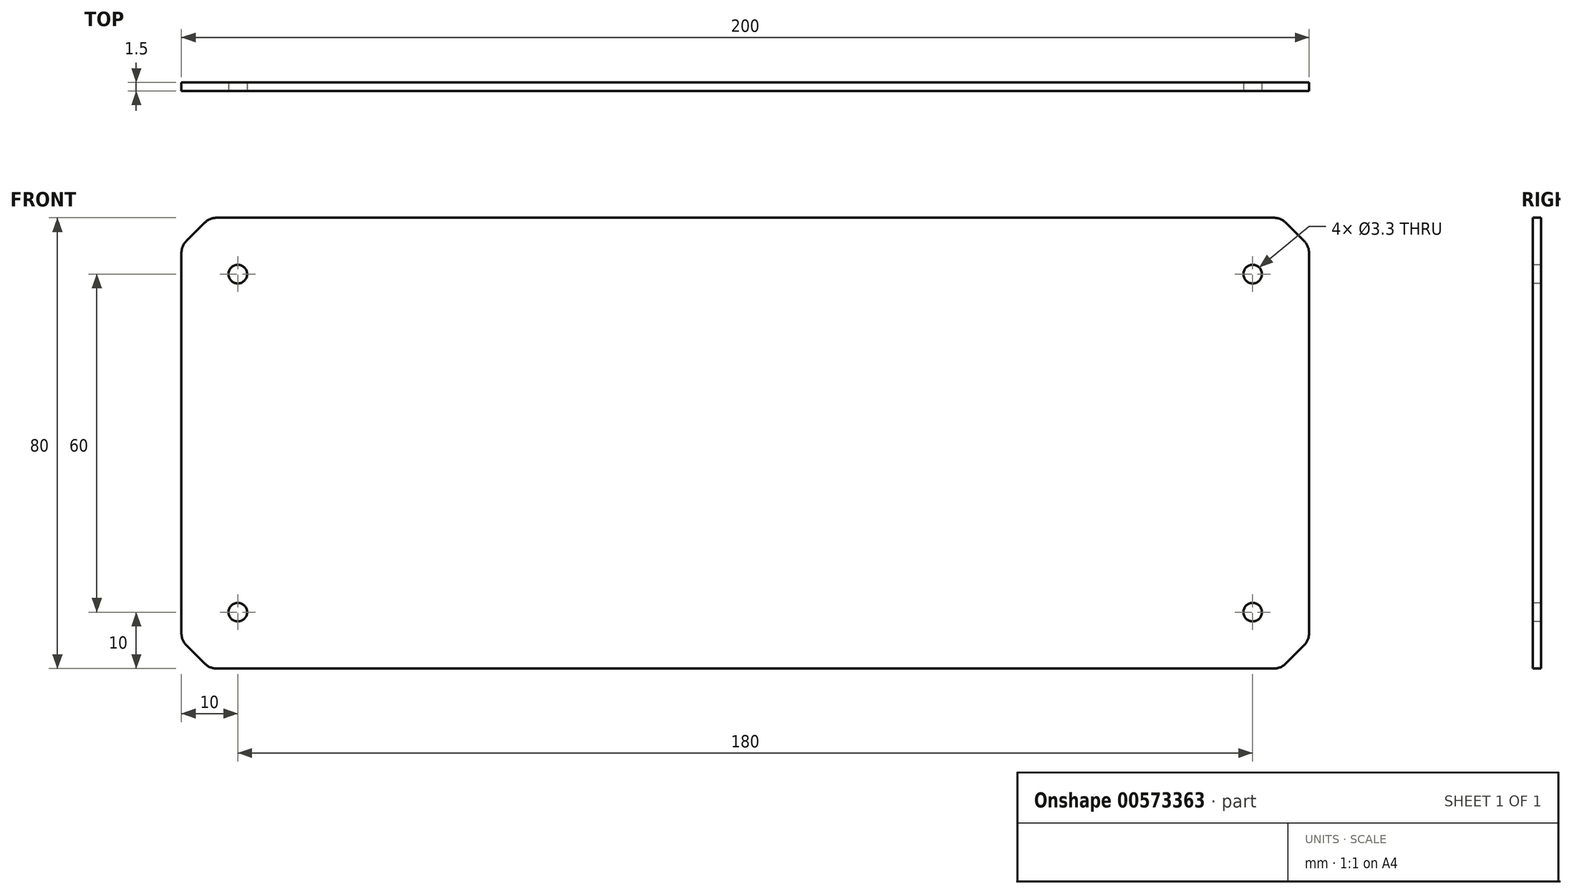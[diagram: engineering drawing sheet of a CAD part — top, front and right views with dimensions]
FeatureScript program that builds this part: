
annotation { "Feature Type Name" : "Feature", "Feature Type Description" : "" }
export const myFeature = defineFeature(function(context is Context, id is Id, definition is map)
    precondition{}
    {
        {
            var Q0;
            Q0=qCreatedBy(makeId("Front.planeOp"),FACE);
            var sketch = newSketch(context, id + "F0", { "sketchPlane" : qUnion([Q0])});
            skLineSegment(sketch, "E0.bottom", {"start": v(100, 40) * mm, "end": v(-100, 40) * mm});
            skLineSegment(sketch, "E0.top", {"start": v(100, -40) * mm, "end": v(-100, -40) * mm});
            skLineSegment(sketch, "E0.left", {"start": v(100, 40) * mm, "end": v(100, -40) * mm});
            skLineSegment(sketch, "E0.right", {"start": v(-100, 40) * mm, "end": v(-100, -40) * mm});
            skPoint(sketch, "E0.middle", {"position": v(0, 0) * mm});
            skSolve(sketch);
        }
        {
            var Q0;
            Q0 = qSketchRegion(id + "F0", true);
            extrude(context, id + "F1", {"entities" : qUnion([Q0]), "depth" : 1.5 * mm, "offsetDistance" : 25.4 * mm});
        }
        {
            var Q0;
            Q0=makeQuery(id+"F1.opExtrude","SWEPT_EDGE",EDGE,{"disambiguationData":[OSD([sQuery(id+"F0.wireOp",EDGE,"E0.bottom"),sQuery(id+"F0.wireOp",EDGE,"E0.left")])]});
            var Q1;
            Q1=makeQuery(id+"F1.opExtrude","SWEPT_EDGE",EDGE,{"disambiguationData":[OSD([sQuery(id+"F0.wireOp",EDGE,"E0.bottom"),sQuery(id+"F0.wireOp",EDGE,"E0.right")])]});
            var Q2;
            Q2=makeQuery(id+"F1.opExtrude","SWEPT_EDGE",EDGE,{"disambiguationData":[OSD([sQuery(id+"F0.wireOp",EDGE,"E0.top"),sQuery(id+"F0.wireOp",EDGE,"E0.right")])]});
            var Q3;
            Q3=makeQuery(id+"F1.opExtrude","SWEPT_EDGE",EDGE,{"disambiguationData":[OSD([sQuery(id+"F0.wireOp",EDGE,"E0.top"),sQuery(id+"F0.wireOp",EDGE,"E0.left")])]});
            chamfer(context, id + "F2", {"entities" : qUnion([Q0, Q1, Q2, Q3]), "width" : 5 * mm, "tangentPropagation" : true});
        }
        {
            var Q0;
            Q0=makeQuery(id+"F1.opExtrude","CAP_FACE",FACE,{"disambiguationData":[OSD([sQuery(id+"F0.wireOp",EDGE,"E0.bottom"),sQuery(id+"F0.wireOp",EDGE,"E0.top"),sQuery(id+"F0.wireOp",EDGE,"E0.left"),sQuery(id+"F0.wireOp",EDGE,"E0.right")])],"isStart":false});
            var sketch = newSketch(context, id + "F3", { "sketchPlane" : qUnion([Q0])});
            skPoint(sketch, "E1", {"position": v(-90, 30) * mm});
            skPoint(sketch, "E2", {"position": v(90, 30) * mm});
            skPoint(sketch, "E3", {"position": v(90, -30) * mm});
            skPoint(sketch, "E4", {"position": v(-90, -30) * mm});
            skSolve(sketch);
        }
        {
            var Q0;
            Q0=sQuery(id+"F3.wireOp",VERTEX,"E1");
            var Q1;
            Q1=sQuery(id+"F3.wireOp",VERTEX,"E4");
            var Q2;
            Q2=sQuery(id+"F3.wireOp",VERTEX,"E3");
            var Q3;
            Q3=sQuery(id+"F3.wireOp",VERTEX,"E2");
            var Q4;
            Q4=makeQuery(id+"F1.opExtrude","SWEPT_BODY",BODY,{"disambiguationData":[OSD([sQuery(id+"F0.wireOp",EDGE,"E0.bottom"),sQuery(id+"F0.wireOp",EDGE,"E0.top"),sQuery(id+"F0.wireOp",EDGE,"E0.left"),sQuery(id+"F0.wireOp",EDGE,"E0.right")])]});
            hole(context, id + "F4", {"style" : HoleStyle.SIMPLE, "endStyle" : HoleEndStyle.THROUGH, "standardTappedOrClearance" : lookupTablePath({ "standard" : "ISO", "fit" : "Normal", "size" : "M3", "type" : "Clearance" }), "standardBlindInLast" : lookupTablePath({ "fit" : "Standard", "standard" : "ISO", "size" : "M3", "type" : "Clearance" }), "holeDiameter" : 3.3 * mm, "isTappedThrough" : true, "tappedDepth" : 12 * mm, "tapClearance" : 3, "locations" : qUnion([Q0, Q1, Q2, Q3]), "scope" : qUnion([Q4])});
        }
        {
            var Q0;
            {var subQ0=sQuery(id+"F0.wireOp",EDGE,"E0.bottom");Q0=makeQuery(id+"F2.opChamfer","BLEND_EDGE",EDGE,{"blendedFrom":[makeQuery(id+"F1.opExtrude","SWEPT_EDGE",EDGE,{"disambiguationData":[OSD([subQ0,sQuery(id+"F0.wireOp",EDGE,"E0.left")])]}),makeQuery(id+"F1.opExtrude","SWEPT_FACE",FACE,{"disambiguationData":[OSD([subQ0])]})],"blendedInto":[makeQuery(id+"F1.opExtrude","SWEPT_FACE",FACE,{"disambiguationData":[OSD([subQ0])]})]});}
            var Q1;
            {var subQ0=sQuery(id+"F0.wireOp",EDGE,"E0.left");Q1=makeQuery(id+"F2.opChamfer","BLEND_EDGE",EDGE,{"blendedFrom":[makeQuery(id+"F1.opExtrude","SWEPT_EDGE",EDGE,{"disambiguationData":[OSD([sQuery(id+"F0.wireOp",EDGE,"E0.bottom"),subQ0])]}),makeQuery(id+"F1.opExtrude","SWEPT_FACE",FACE,{"disambiguationData":[OSD([subQ0])]})],"blendedInto":[makeQuery(id+"F1.opExtrude","SWEPT_FACE",FACE,{"disambiguationData":[OSD([subQ0])]})]});}
            var Q2;
            {var subQ0=sQuery(id+"F0.wireOp",EDGE,"E0.left");Q2=makeQuery(id+"F2.opChamfer","BLEND_EDGE",EDGE,{"blendedFrom":[makeQuery(id+"F1.opExtrude","SWEPT_EDGE",EDGE,{"disambiguationData":[OSD([sQuery(id+"F0.wireOp",EDGE,"E0.top"),subQ0])]}),makeQuery(id+"F1.opExtrude","SWEPT_FACE",FACE,{"disambiguationData":[OSD([subQ0])]})],"blendedInto":[makeQuery(id+"F1.opExtrude","SWEPT_FACE",FACE,{"disambiguationData":[OSD([subQ0])]})]});}
            var Q3;
            {var subQ0=sQuery(id+"F0.wireOp",EDGE,"E0.top");Q3=makeQuery(id+"F2.opChamfer","BLEND_EDGE",EDGE,{"blendedFrom":[makeQuery(id+"F1.opExtrude","SWEPT_EDGE",EDGE,{"disambiguationData":[OSD([subQ0,sQuery(id+"F0.wireOp",EDGE,"E0.left")])]}),makeQuery(id+"F1.opExtrude","SWEPT_FACE",FACE,{"disambiguationData":[OSD([subQ0])]})],"blendedInto":[makeQuery(id+"F1.opExtrude","SWEPT_FACE",FACE,{"disambiguationData":[OSD([subQ0])]})]});}
            var Q4;
            {var subQ0=sQuery(id+"F0.wireOp",EDGE,"E0.top");Q4=makeQuery(id+"F2.opChamfer","BLEND_EDGE",EDGE,{"blendedFrom":[makeQuery(id+"F1.opExtrude","SWEPT_EDGE",EDGE,{"disambiguationData":[OSD([subQ0,sQuery(id+"F0.wireOp",EDGE,"E0.right")])]}),makeQuery(id+"F1.opExtrude","SWEPT_FACE",FACE,{"disambiguationData":[OSD([subQ0])]})],"blendedInto":[makeQuery(id+"F1.opExtrude","SWEPT_FACE",FACE,{"disambiguationData":[OSD([subQ0])]})]});}
            var Q5;
            {var subQ0=sQuery(id+"F0.wireOp",EDGE,"E0.right");Q5=makeQuery(id+"F2.opChamfer","BLEND_EDGE",EDGE,{"blendedFrom":[makeQuery(id+"F1.opExtrude","SWEPT_EDGE",EDGE,{"disambiguationData":[OSD([sQuery(id+"F0.wireOp",EDGE,"E0.top"),subQ0])]}),makeQuery(id+"F1.opExtrude","SWEPT_FACE",FACE,{"disambiguationData":[OSD([subQ0])]})],"blendedInto":[makeQuery(id+"F1.opExtrude","SWEPT_FACE",FACE,{"disambiguationData":[OSD([subQ0])]})]});}
            var Q6;
            {var subQ0=sQuery(id+"F0.wireOp",EDGE,"E0.right");Q6=makeQuery(id+"F2.opChamfer","BLEND_EDGE",EDGE,{"blendedFrom":[makeQuery(id+"F1.opExtrude","SWEPT_EDGE",EDGE,{"disambiguationData":[OSD([sQuery(id+"F0.wireOp",EDGE,"E0.bottom"),subQ0])]}),makeQuery(id+"F1.opExtrude","SWEPT_FACE",FACE,{"disambiguationData":[OSD([subQ0])]})],"blendedInto":[makeQuery(id+"F1.opExtrude","SWEPT_FACE",FACE,{"disambiguationData":[OSD([subQ0])]})]});}
            var Q7;
            {var subQ0=sQuery(id+"F0.wireOp",EDGE,"E0.bottom");Q7=makeQuery(id+"F2.opChamfer","BLEND_EDGE",EDGE,{"blendedFrom":[makeQuery(id+"F1.opExtrude","SWEPT_EDGE",EDGE,{"disambiguationData":[OSD([subQ0,sQuery(id+"F0.wireOp",EDGE,"E0.right")])]}),makeQuery(id+"F1.opExtrude","SWEPT_FACE",FACE,{"disambiguationData":[OSD([subQ0])]})],"blendedInto":[makeQuery(id+"F1.opExtrude","SWEPT_FACE",FACE,{"disambiguationData":[OSD([subQ0])]})]});}
            fillet(context, id + "F5", {"entities" : qUnion([Q0, Q1, Q2, Q3, Q4, Q5, Q6, Q7]), "radius" : 3 * mm, "tangentPropagation" : true, "allowEdgeOverflow" : false});
        }
    });
